# Revit family: FU_Inspec_A22_4-2
name_source: partatom
category: Furniture
units: mm (PartAtom-declared; Revit-internal decimal feet)

## family parameters
Always vertical = Yes
Cut with Voids When Loaded = No
OmniClass Number = 23.40.20.00
OmniClass Title = General Furniture and Specialties
Room Calculation Point = No
Shared = No
Work Plane-Based = No

## types (2) — shared parameters
Assembly Code = E2020
Depth = 400 mm  [stored 1.31234 ft]
Description = Counterstool. Frame of Ø 25 & 20 mm powder coated steel tube. Seat of 3mm perforated sheet steel. Loose reversible cushion as an option. Glides. Stackable.
Height = 670 mm  [stored 2.19816 ft]
Keynote = 46.B
Manufacturer = Inspec
Model = A22 4.2
Seat Material = <By Category>
URL = https://inspecfurniture.com
Weight = 6.5kg
Width = 540 mm  [stored 1.77165 ft]
zero-valued in all types: Default Elevation

## per-type parameters (varying)
| type | Frame Material | Material_temp | Seat Pad Material |
| A22 4.2 - White - Seat Pad | Metal - White - Matte | Metal - Black - Matte | Fabric - Beige |
| A22 4.2 - Graphite - No Seat Pad | Metal - Graphite - Matte | Metal - Graphite - Matte | Metal - Black - Matte |

note: [stored X ft] marks values corroborated as IEEE doubles in the binary element streams (Revit-internal decimal feet)

## geometry (parser evidence)
native form markers: Blend x4, Sweep x2
no freeform markers — native parametric forms only
